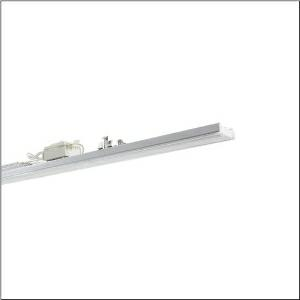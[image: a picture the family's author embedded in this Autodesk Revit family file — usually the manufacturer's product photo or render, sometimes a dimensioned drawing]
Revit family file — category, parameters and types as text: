
# Revit family: licross_r__11_recessed_mo_51te10mn4axg_50db
name_source: partatom
category: Lighting Fixtures
units: mm (PartAtom-declared; Revit-internal decimal feet)

## family parameters
Cut with Voids When Loaded = No
Host = Face
Light Source = No
Part Type = Normal
Room Calculation Point = No
Round Connector Dimension = Use Diameter
Shared = No

## types (1)
- --- (1 x LED, 10000 lm, 55.2 W, 4000K)
    Apparent Load = 55 VA
    CIE Flux Codes = 50 81 96 100 100
    Color Rendering = 80
    Color Temperature = 4000K
    Default Elevation = 1800 mm
    Description = Licross® 11 Recessed MO, luminaire insert, of sheet steel, galvanised, coil coated, white, length: 1.500mm, width: 66mm, height: 67mm, LED rated luminous flux: 10.000lm, light colour: 840, control gear: ON/OFF Multilumen, with plug, 3-pole, with phase selection, mains connection: 220..240V, AC, 50/60Hz, rated input power: 55W, halogen-free wiring, primary optical cover: cover, of PMMA, light emission: direct distribution, primary light characteristic: symmetric, protection rating (complete): IP54, insulation class (complete): insulation class I (protective earthing), certification: CE, ENEC, VDE, UKCA, protection symbol: D if used in an environment with non-conductive dust loads with corresponding accessories, impact resistance: IK06, permissible ambient temperature for indoor applications: -35..+40°C, corresponds to IFS (International Featured Standards) requirements for safety and quality in the food industry, reducing of maximum allowable ambient temperature of 5°C with ceiling mounting, packaging unit: 1 piece
    Height = 58 mm
    Lamp = 1 x LED
    Lamp Light Flux = 10000 lm
    Lamp Power = 55.2 W
    Lamp count = 1
    Length = 1500 mm
    Luminous efficacy = 181 lm/W
    Manufacturer = Siteco
    ModVariant = No
    Model = 51TE10MN4AXG
    Mounting Place = Ceiling
    Mounting Type = Pendant
    Number of Poles = 1
    OnlyDefault = Yes
    Power Factor = 1
    Product Name = Licross® 11 Recessed MO
    Product group = luminaire insert
    ProductGroupID = 902
    Protection Class = Protection class I
    Protection Degree = IP 54
    RLX_Detail_Level = 1
    RLX_Emergency_Light_Flux = 0 lm
    RLX_Emergency_Type = 0
    RLX_Emergency_Type_DB = No
    RlxData = <blob elided: 22085 chars, md5=7d213bf9>
    Socket = socket
    Standby Power = 0 W
    System Light Flux = 10000 lm
    System Power = 55 W
    Type Comments = factory setting: luminous flux: 100 % | (A | C | E) | 126 mA
    Type Image = l_1296930.jpg
    URL = http://relux.com
    VarID = @adj_085172
    Voltage = 0 V
    Weight = 0.00 kg
    Width = 66 mm

## geometry (parser evidence)
native form markers: Blend x4, Sweep x10
no freeform markers — native parametric forms only
